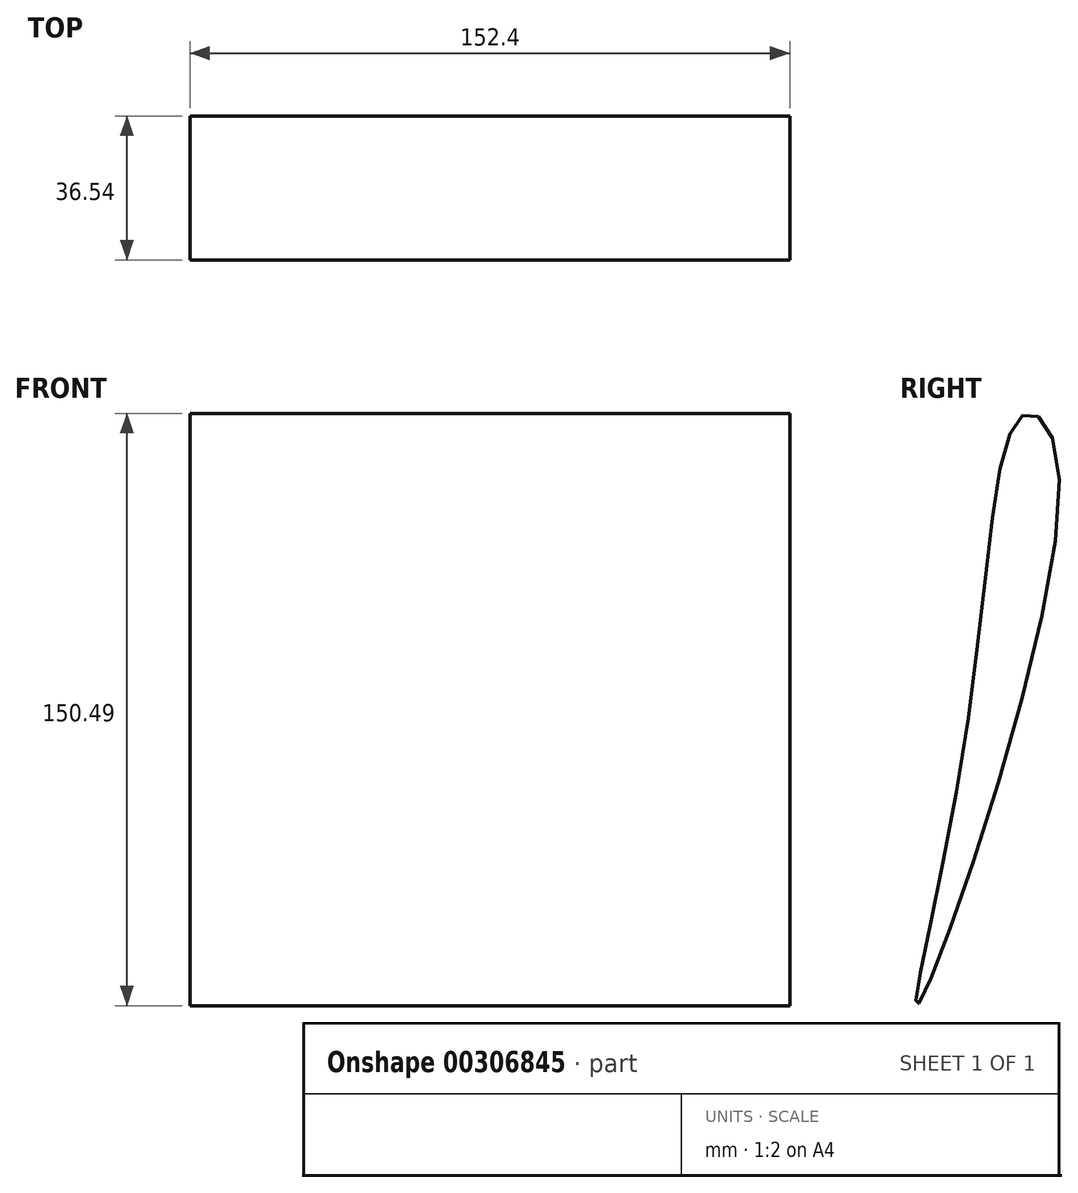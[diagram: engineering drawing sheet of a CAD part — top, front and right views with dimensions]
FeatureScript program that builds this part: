
annotation { "Feature Type Name" : "Feature", "Feature Type Description" : "" }
export const myFeature = defineFeature(function(context is Context, id is Id, definition is map)
    precondition{}
    {
        {
            var Q0;
            Q0=qCreatedBy(makeId("Right.planeOp"),FACE);
            var sketch = newSketch(context, id + "F0", { "sketchPlane" : qUnion([Q0])});
            skFitSpline(sketch, "E0", {"points": [v(24.33, 73.03) * mm, v(33.67, 58.14) * mm, v(-2.03, -76.46) * mm, v(9.72, -9.8) * mm, v(24.33, 73.03) * mm]});
            skSolve(sketch);
        }
        {
            var Q0;
            Q0=makeQuery(id+"F0.imprint","IMPRINT",FACE,{"disambiguationData":[TD([[makeQuery(id+"F0.imprint","IMPRINT",EDGE,{"derivedFrom":sQuery(id+"F0.wireOp",EDGE,"E0")}),-1.0]])]});
            extrude(context, id + "F1", {"entities" : qUnion([Q0]), "depth" : 76.2 * mm, "hasSecondDirection" : true, "secondDirectionOppositeDirection" : true, "secondDirectionDepth" : 76.2 * mm});
        }
    });
